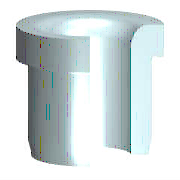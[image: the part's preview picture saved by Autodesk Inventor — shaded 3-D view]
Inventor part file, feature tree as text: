
AUTODESK INVENTOR PART (.ipt)
format: ipt  version: 2023.3 (Build 273359000, 359)  size: 183,296 bytes
history: native  units: mm (DEFAULTED — no unit token found)
features: other x1, plane x1, hole x1, sketch x1
ambient origin geometry x8: Origin, YZ Plane, XZ Plane, XY Plane, X Axis, Y Axis, Z Axis, Center Point
bodies: Solid1 (feature_tree)
feature tree (4):
  other  "Körper"
  plane  "Arbeitsebene1"
  hole  "Bohrung1"  [1 undecoded]
  sketch  "Skizze2"  dims[d0=11.0mm d1=8.0mm d2=12.0mm d3=2.094395mm d4=0.4mm d5=0.1mm d6=2.0mm d7=15.0deg d8=0.2mm d9=0.4mm d10=2.5mm d11=5.0mm d22=90.0deg d12=1.0mm d13=15.0deg d14=1.0mm d15=0.0mm d16=0.0mm d17=0.0mm d29=1.0mm d30=3.0mm d32=0.5mm d33=6.0mm d34=1.0mm d35=2.0mm d36=3.490659mm d37=8.0mm d38=20.594885mm d39=6.0mm]
note: 1 required parameter value undecoded (feature->parameter linkage not recoverable at this tier; creation-order binding heuristic only, values carry confidence <= 0.55)
